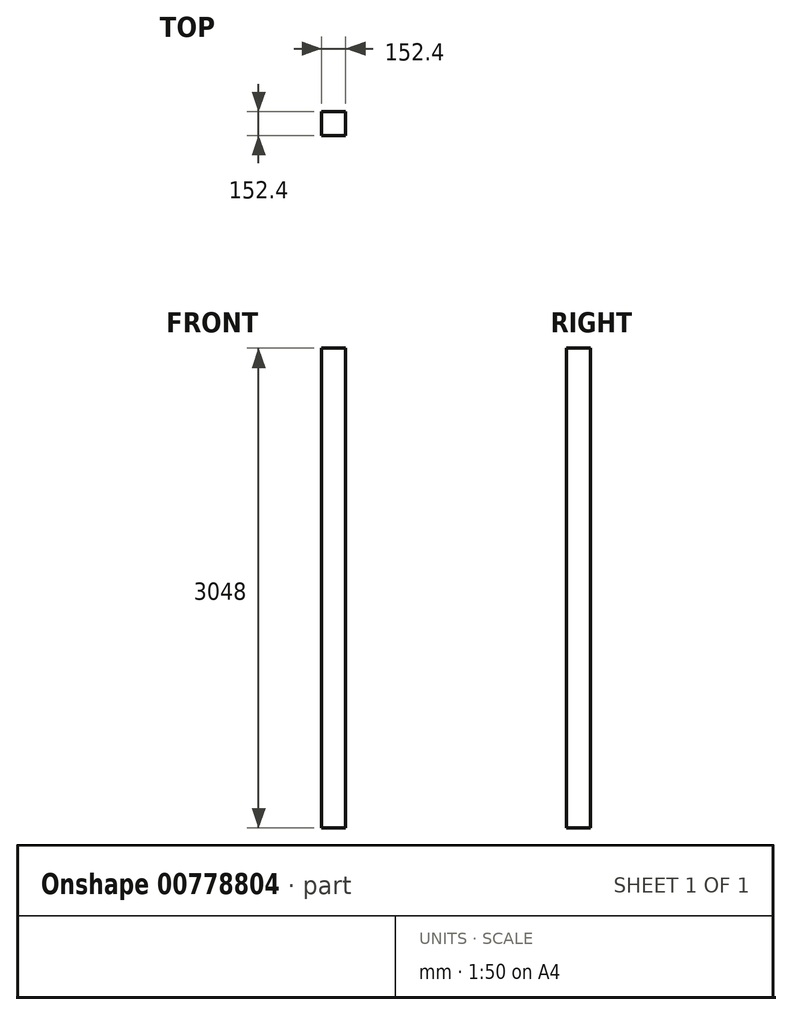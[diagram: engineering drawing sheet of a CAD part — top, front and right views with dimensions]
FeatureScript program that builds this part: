
annotation { "Feature Type Name" : "Feature", "Feature Type Description" : "" }
export const myFeature = defineFeature(function(context is Context, id is Id, definition is map)
    precondition{}
    {
        {
            var Q0;
            Q0=qCreatedBy(makeId("Top.planeOp"),FACE);
            var sketch = newSketch(context, id + "F0", { "sketchPlane" : qUnion([Q0])});
            skLineSegment(sketch, "E0.bottom", {"start": v(0, 0) * mm, "end": v(152.4, 0) * mm});
            skLineSegment(sketch, "E0.top", {"start": v(0, 152.4) * mm, "end": v(152.4, 152.4) * mm});
            skLineSegment(sketch, "E0.left", {"start": v(0, 0) * mm, "end": v(0, 152.4) * mm});
            skLineSegment(sketch, "E0.right", {"start": v(152.4, 0) * mm, "end": v(152.4, 152.4) * mm});
            skSolve(sketch);
        }
        {
            var Q0;
            Q0=makeQuery(id+"F0.imprint","IMPRINT",FACE,{"disambiguationData":[TD([[makeQuery(id+"F0.imprint","IMPRINT",EDGE,{"derivedFrom":sQuery(id+"F0.wireOp",EDGE,"E0.bottom")}),1.0]])]});
            extrude(context, id + "F1", {"entities" : qUnion([Q0]), "depth" : 3048 * mm, "offsetDistance" : 25.4 * mm});
        }
    });
